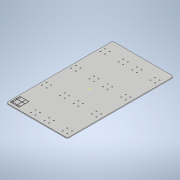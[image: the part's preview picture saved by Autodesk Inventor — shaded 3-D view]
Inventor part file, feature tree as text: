
AUTODESK INVENTOR PART (.ipt)
format: ipt  version: 2022 (Build 260153000, 153)  size: 290,816 bytes
history: native  units: in
note: dims shown in document units (in); Inventor stores cm internally (conversion verified against a paired STEP export)
features: sketch x4, extrude x3, fillet x1
ambient origin geometry x8: Origin, YZ Plane, XZ Plane, XY Plane, X Axis, Y Axis, Z Axis, Center Point
bodies: Solid1 (feature_tree)
feature tree (8):
  extrude  "Extrusion1"  Depth=8.2244in
  fillet  "Fillet1"  Radius=0.0625in
  extrude  "Extrusion2"  Depth=0.1575in
  sketch  "Sketch4"  dims[d32=0.3543in d33=0.3543in]
  extrude  "Extrusion3"  Depth=0.3543in
  sketch  "Sketch1"  dims[d0=4.7244in d1=8.2244in d2=0.0625in d3=0.0in]
  sketch  "Sketch3"  dims[d29=0.1575in d31=0.0787in]
  sketch  "Sketch5"  dims[d34=0.2165in d35=0.2953in d36=1.5748in d38=2.2566in d39=0.7874in d41=1.4002in d44=0.0787in d45=0.3543in d46=0.3543in d47=0.2953in d48=0.2953in d49=1.5748in d51=2.2566in d52=0.7874in d54=1.4002in d57=0.0in d58=0.0in d59=0.6988in d60=0.7697in d61=0.1033in d62=0.312in d63=0.1033in d64=0.0197in d65=0.0197in d66=0.0197in d67=0.0197in d68=0.0394in d69=0.0in d70=0.0197in d71=0.0197in d72=0.0197in d73=0.0197in d74=0.0098in d75=0.0098in d76=0.0098in d77=0.0098in]
